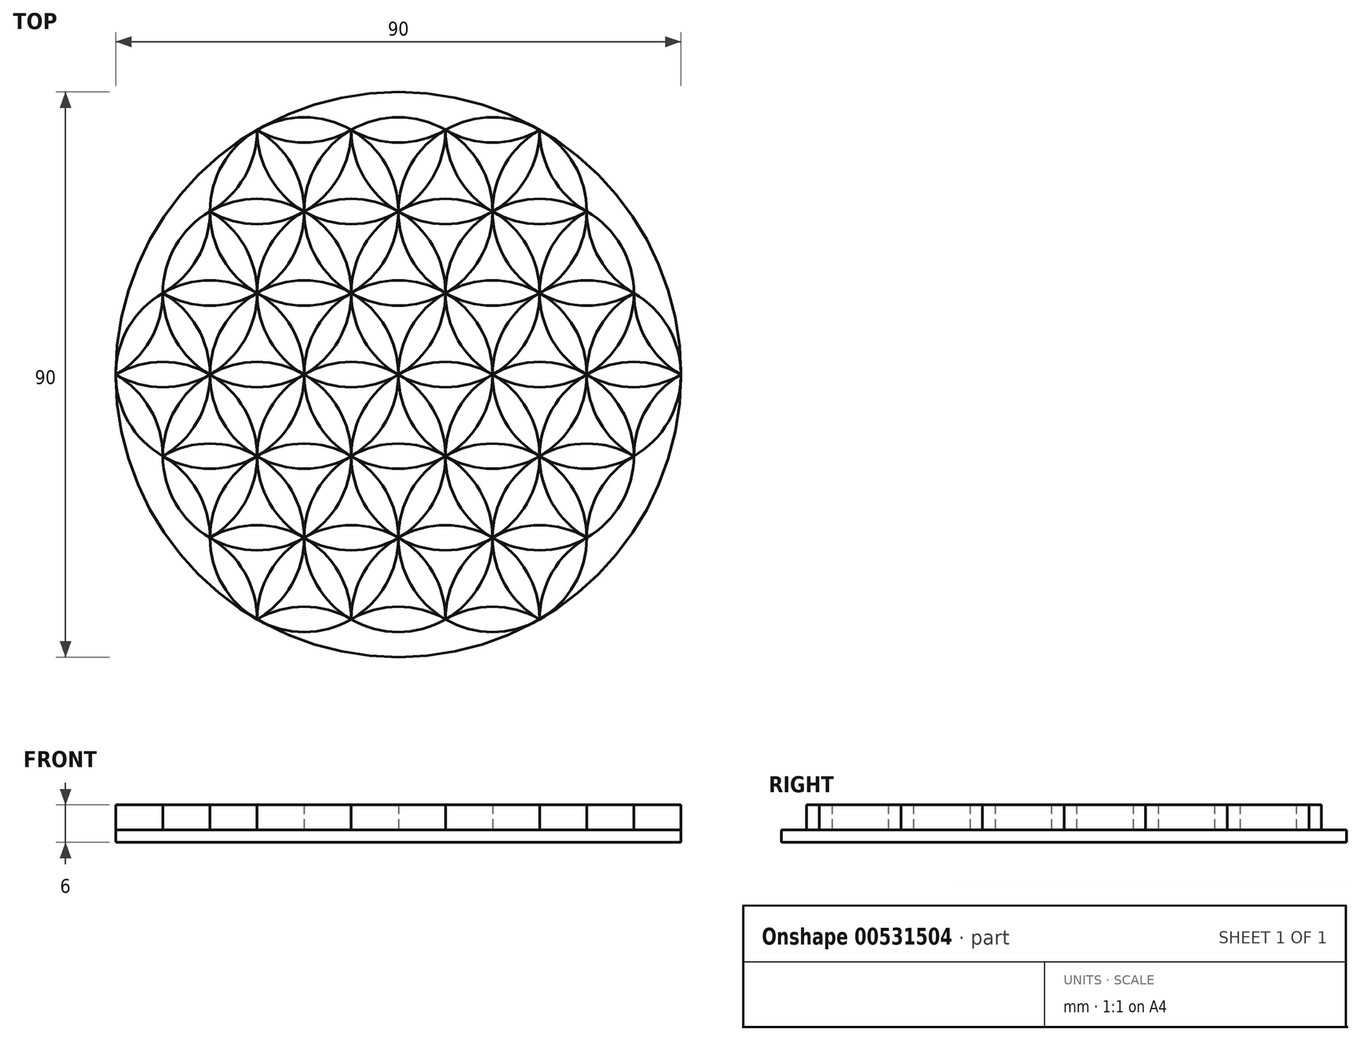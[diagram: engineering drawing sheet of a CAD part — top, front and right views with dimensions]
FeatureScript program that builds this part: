
annotation { "Feature Type Name" : "Feature", "Feature Type Description" : "" }
export const myFeature = defineFeature(function(context is Context, id is Id, definition is map)
    precondition{}
    {
        {
            var Q0;
            Q0=qCreatedBy(makeId("Top.planeOp"),FACE);
            var sketch = newSketch(context, id + "F0", { "sketchPlane" : qUnion([Q0])});
            skCircle(sketch, "E0", {"center": v(0, 0) * mm, "radius": 15 * mm});
            skCircle(sketch, "E1", {"center": v(15, 0) * mm, "radius": 15 * mm});
            skCircle(sketch, "E2", {"center": v(7.5, -13) * mm, "radius": 15 * mm});
            skCircle(sketch, "E3", {"center": v(-7.5, -13) * mm, "radius": 15 * mm});
            skCircle(sketch, "E4", {"center": v(-15, 0) * mm, "radius": 15 * mm});
            skCircle(sketch, "E5", {"center": v(-7.5, 13) * mm, "radius": 15 * mm});
            skCircle(sketch, "E6", {"center": v(7.5, 13) * mm, "radius": 15 * mm});
            skCircle(sketch, "E7", {"center": v(22.5, 13) * mm, "radius": 15 * mm});
            skCircle(sketch, "E8", {"center": v(-22.5, 13) * mm, "radius": 15 * mm});
            skCircle(sketch, "E9", {"center": v(-22.5, -13) * mm, "radius": 15 * mm});
            skCircle(sketch, "E10", {"center": v(-15, 25.98) * mm, "radius": 15 * mm});
            skCircle(sketch, "E11", {"center": v(0, 25.98) * mm, "radius": 15 * mm});
            skCircle(sketch, "E12", {"center": v(15, 25.98) * mm, "radius": 15 * mm});
            skCircle(sketch, "E13", {"center": v(7.5, 38.97) * mm, "radius": 15 * mm});
            skCircle(sketch, "E14", {"center": v(-7.5, 38.97) * mm, "radius": 15 * mm});
            skCircle(sketch, "E15", {"center": v(22.5, -13) * mm, "radius": 15 * mm});
            skCircle(sketch, "E16", {"center": v(30, 0) * mm, "radius": 15 * mm});
            skCircle(sketch, "E17", {"center": v(-30, 0) * mm, "radius": 15 * mm});
            skCircle(sketch, "E18", {"center": v(-15, -25.98) * mm, "radius": 15 * mm});
            skCircle(sketch, "E19", {"center": v(0, -25.98) * mm, "radius": 15 * mm});
            skCircle(sketch, "E20", {"center": v(15, -25.98) * mm, "radius": 15 * mm});
            skCircle(sketch, "E21", {"center": v(7.5, -38.97) * mm, "radius": 15 * mm});
            skCircle(sketch, "E22", {"center": v(-7.5, -38.97) * mm, "radius": 15 * mm});
            skCircle(sketch, "E23", {"center": v(30, -25.98) * mm, "radius": 15 * mm});
            skCircle(sketch, "E24", {"center": v(37.5, -13) * mm, "radius": 15 * mm});
            skCircle(sketch, "E25", {"center": v(-30, -25.98) * mm, "radius": 15 * mm});
            skCircle(sketch, "E26", {"center": v(-37.5, -13) * mm, "radius": 15 * mm});
            skCircle(sketch, "E27", {"center": v(-22.5, -38.97) * mm, "radius": 15 * mm});
            skCircle(sketch, "E28", {"center": v(22.5, -38.97) * mm, "radius": 15 * mm});
            skCircle(sketch, "E29", {"center": v(30, 25.98) * mm, "radius": 15 * mm});
            skCircle(sketch, "E30", {"center": v(37.5, 13) * mm, "radius": 15 * mm});
            skCircle(sketch, "E31", {"center": v(-30, 25.98) * mm, "radius": 15 * mm});
            skCircle(sketch, "E32", {"center": v(-37.5, 13) * mm, "radius": 15 * mm});
            skCircle(sketch, "E33", {"center": v(45, 0) * mm, "radius": 15 * mm});
            skCircle(sketch, "E34", {"center": v(45, -25.98) * mm, "radius": 15 * mm});
            skCircle(sketch, "E35", {"center": v(0, -51.96) * mm, "radius": 15 * mm});
            skCircle(sketch, "E36", {"center": v(0, 51.96) * mm, "radius": 15 * mm});
            skCircle(sketch, "E37", {"center": v(22.5, 38.97) * mm, "radius": 15 * mm});
            skCircle(sketch, "E38", {"center": v(-22.5, 38.97) * mm, "radius": 15 * mm});
            skCircle(sketch, "E39", {"center": v(-45, 0) * mm, "radius": 15 * mm});
            skCircle(sketch, "E40", {"center": v(-15, -51.96) * mm, "radius": 15 * mm});
            skCircle(sketch, "E41", {"center": v(15, -51.96) * mm, "radius": 15 * mm});
            skCircle(sketch, "E42", {"center": v(-45, -25.98) * mm, "radius": 15 * mm});
            skCircle(sketch, "E43", {"center": v(-37.5, -38.97) * mm, "radius": 15 * mm});
            skCircle(sketch, "E44", {"center": v(-52.5, 13) * mm, "radius": 15 * mm});
            skCircle(sketch, "E45", {"center": v(-45, 25.98) * mm, "radius": 15 * mm});
            skCircle(sketch, "E46", {"center": v(-37.5, 38.97) * mm, "radius": 15 * mm});
            skCircle(sketch, "E47", {"center": v(37.5, -38.97) * mm, "radius": 15 * mm});
            skCircle(sketch, "E48", {"center": v(-15, 51.96) * mm, "radius": 15 * mm});
            skCircle(sketch, "E49", {"center": v(-52.5, -13) * mm, "radius": 15 * mm});
            skCircle(sketch, "E50", {"center": v(15, 51.96) * mm, "radius": 15 * mm});
            skCircle(sketch, "E51", {"center": v(52.5, -13) * mm, "radius": 15 * mm});
            skCircle(sketch, "E52", {"center": v(37.5, 38.97) * mm, "radius": 15 * mm});
            skCircle(sketch, "E53", {"center": v(45, 25.98) * mm, "radius": 15 * mm});
            skCircle(sketch, "E54", {"center": v(52.5, 13) * mm, "radius": 15 * mm});
            skSolve(sketch);
        }
        {
            var Q0;
            {var subQ0=sQuery(id+"F0.wireOp",EDGE,"E6");var subQ1=sQuery(id+"F0.wireOp",EDGE,"E2");var subQ2=makeQuery(id+"F0.imprint","INTERSECT",VERTEX,{"derivedFrom":[sQuery(id+"F0.wireOp",EDGE,"E0"),subQ1,subQ0,sQuery(id+"F0.wireOp",EDGE,"E7"),sQuery(id+"F0.wireOp",EDGE,"E15"),sQuery(id+"F0.wireOp",EDGE,"E16")]});Q0=makeQuery(id+"F0.imprint","IMPRINT",FACE,{"disambiguationData":[TD([[makeQuery(id+"F0.imprint","IMPRINT",EDGE,{"disambiguationData":[TD([[subQ2,-1.0]])],"derivedFrom":subQ1}),1.0]])]});}
            var Q1;
            {var subQ0=sQuery(id+"F0.wireOp",EDGE,"E5");var subQ1=sQuery(id+"F0.wireOp",EDGE,"E1");var subQ2=makeQuery(id+"F0.imprint","INTERSECT",VERTEX,{"derivedFrom":[sQuery(id+"F0.wireOp",EDGE,"E0"),subQ1,subQ0,sQuery(id+"F0.wireOp",EDGE,"E7"),sQuery(id+"F0.wireOp",EDGE,"E11"),sQuery(id+"F0.wireOp",EDGE,"E12")]});Q1=makeQuery(id+"F0.imprint","IMPRINT",FACE,{"disambiguationData":[TD([[makeQuery(id+"F0.imprint","IMPRINT",EDGE,{"disambiguationData":[TD([[subQ2,-1.0]])],"derivedFrom":subQ1}),1.0]])]});}
            var Q2;
            {var subQ0=sQuery(id+"F0.wireOp",EDGE,"E6");var subQ1=sQuery(id+"F0.wireOp",EDGE,"E4");var subQ2=makeQuery(id+"F0.imprint","INTERSECT",VERTEX,{"derivedFrom":[sQuery(id+"F0.wireOp",EDGE,"E0"),subQ1,subQ0,sQuery(id+"F0.wireOp",EDGE,"E8"),sQuery(id+"F0.wireOp",EDGE,"E10"),sQuery(id+"F0.wireOp",EDGE,"E11")]});Q2=makeQuery(id+"F0.imprint","IMPRINT",FACE,{"disambiguationData":[TD([[makeQuery(id+"F0.imprint","IMPRINT",EDGE,{"disambiguationData":[TD([[subQ2,1.0]])],"derivedFrom":subQ1}),1.0]])]});}
            var Q3;
            {var subQ0=sQuery(id+"F0.wireOp",EDGE,"E5");var subQ1=sQuery(id+"F0.wireOp",EDGE,"E3");var subQ2=makeQuery(id+"F0.imprint","INTERSECT",VERTEX,{"derivedFrom":[sQuery(id+"F0.wireOp",EDGE,"E0"),subQ1,subQ0,sQuery(id+"F0.wireOp",EDGE,"E8"),sQuery(id+"F0.wireOp",EDGE,"E9"),sQuery(id+"F0.wireOp",EDGE,"E17")]});Q3=makeQuery(id+"F0.imprint","IMPRINT",FACE,{"disambiguationData":[TD([[makeQuery(id+"F0.imprint","IMPRINT",EDGE,{"disambiguationData":[TD([[subQ2,1.0]])],"derivedFrom":subQ1}),1.0]])]});}
            var Q4;
            {var subQ0=sQuery(id+"F0.wireOp",EDGE,"E4");var subQ1=sQuery(id+"F0.wireOp",EDGE,"E2");var subQ2=makeQuery(id+"F0.imprint","INTERSECT",VERTEX,{"derivedFrom":[sQuery(id+"F0.wireOp",EDGE,"E0"),subQ1,subQ0,sQuery(id+"F0.wireOp",EDGE,"E9"),sQuery(id+"F0.wireOp",EDGE,"E18"),sQuery(id+"F0.wireOp",EDGE,"E19")]});Q4=makeQuery(id+"F0.imprint","IMPRINT",FACE,{"disambiguationData":[TD([[makeQuery(id+"F0.imprint","IMPRINT",EDGE,{"disambiguationData":[TD([[subQ2,1.0]])],"derivedFrom":subQ1}),1.0]])]});}
            var Q5;
            {var subQ0=sQuery(id+"F0.wireOp",EDGE,"E3");var subQ1=sQuery(id+"F0.wireOp",EDGE,"E1");var subQ2=makeQuery(id+"F0.imprint","INTERSECT",VERTEX,{"derivedFrom":[sQuery(id+"F0.wireOp",EDGE,"E0"),subQ1,subQ0,sQuery(id+"F0.wireOp",EDGE,"E15"),sQuery(id+"F0.wireOp",EDGE,"E19"),sQuery(id+"F0.wireOp",EDGE,"E20")]});Q5=makeQuery(id+"F0.imprint","IMPRINT",FACE,{"disambiguationData":[TD([[makeQuery(id+"F0.imprint","IMPRINT",EDGE,{"disambiguationData":[TD([[subQ2,1.0]])],"derivedFrom":subQ1}),1.0]])]});}
            var Q6;
            {var subQ0=sQuery(id+"F0.wireOp",EDGE,"E15");var subQ1=sQuery(id+"F0.wireOp",EDGE,"E0");var subQ2=makeQuery(id+"F0.imprint","INTERSECT",VERTEX,{"derivedFrom":[subQ1,sQuery(id+"F0.wireOp",EDGE,"E2"),sQuery(id+"F0.wireOp",EDGE,"E6"),sQuery(id+"F0.wireOp",EDGE,"E7"),subQ0,sQuery(id+"F0.wireOp",EDGE,"E16")]});Q6=makeQuery(id+"F0.imprint","IMPRINT",FACE,{"disambiguationData":[TD([[makeQuery(id+"F0.imprint","IMPRINT",EDGE,{"disambiguationData":[TD([[subQ2,1.0]])],"derivedFrom":subQ1}),1.0]])]});}
            var Q7;
            {var subQ0=sQuery(id+"F0.wireOp",EDGE,"E7");var subQ1=sQuery(id+"F0.wireOp",EDGE,"E0");var subQ2=makeQuery(id+"F0.imprint","INTERSECT",VERTEX,{"derivedFrom":[subQ1,sQuery(id+"F0.wireOp",EDGE,"E1"),sQuery(id+"F0.wireOp",EDGE,"E5"),subQ0,sQuery(id+"F0.wireOp",EDGE,"E11"),sQuery(id+"F0.wireOp",EDGE,"E12")]});Q7=makeQuery(id+"F0.imprint","IMPRINT",FACE,{"disambiguationData":[TD([[makeQuery(id+"F0.imprint","IMPRINT",EDGE,{"disambiguationData":[TD([[subQ2,1.0]])],"derivedFrom":subQ1}),1.0]])]});}
            var Q8;
            {var subQ0=sQuery(id+"F0.wireOp",EDGE,"E11");var subQ1=sQuery(id+"F0.wireOp",EDGE,"E0");var subQ2=makeQuery(id+"F0.imprint","INTERSECT",VERTEX,{"derivedFrom":[subQ1,sQuery(id+"F0.wireOp",EDGE,"E1"),sQuery(id+"F0.wireOp",EDGE,"E5"),sQuery(id+"F0.wireOp",EDGE,"E7"),subQ0,sQuery(id+"F0.wireOp",EDGE,"E12")]});Q8=makeQuery(id+"F0.imprint","IMPRINT",FACE,{"disambiguationData":[TD([[makeQuery(id+"F0.imprint","IMPRINT",EDGE,{"disambiguationData":[TD([[subQ2,-1.0]])],"derivedFrom":subQ1}),1.0]])]});}
            var Q9;
            {var subQ0=sQuery(id+"F0.wireOp",EDGE,"E8");var subQ1=sQuery(id+"F0.wireOp",EDGE,"E0");var subQ2=makeQuery(id+"F0.imprint","INTERSECT",VERTEX,{"derivedFrom":[subQ1,sQuery(id+"F0.wireOp",EDGE,"E4"),sQuery(id+"F0.wireOp",EDGE,"E6"),subQ0,sQuery(id+"F0.wireOp",EDGE,"E10"),sQuery(id+"F0.wireOp",EDGE,"E11")]});Q9=makeQuery(id+"F0.imprint","IMPRINT",FACE,{"disambiguationData":[TD([[makeQuery(id+"F0.imprint","IMPRINT",EDGE,{"disambiguationData":[TD([[subQ2,-1.0]])],"derivedFrom":subQ1}),1.0]])]});}
            var Q10;
            {var subQ0=sQuery(id+"F0.wireOp",EDGE,"E9");var subQ1=sQuery(id+"F0.wireOp",EDGE,"E0");var subQ2=makeQuery(id+"F0.imprint","INTERSECT",VERTEX,{"derivedFrom":[subQ1,sQuery(id+"F0.wireOp",EDGE,"E3"),sQuery(id+"F0.wireOp",EDGE,"E5"),sQuery(id+"F0.wireOp",EDGE,"E8"),subQ0,sQuery(id+"F0.wireOp",EDGE,"E17")]});Q10=makeQuery(id+"F0.imprint","IMPRINT",FACE,{"disambiguationData":[TD([[makeQuery(id+"F0.imprint","IMPRINT",EDGE,{"disambiguationData":[TD([[subQ2,-1.0]])],"derivedFrom":subQ1}),1.0]])]});}
            var Q11;
            {var subQ0=sQuery(id+"F0.wireOp",EDGE,"E19");var subQ1=sQuery(id+"F0.wireOp",EDGE,"E0");var subQ2=makeQuery(id+"F0.imprint","INTERSECT",VERTEX,{"derivedFrom":[subQ1,sQuery(id+"F0.wireOp",EDGE,"E2"),sQuery(id+"F0.wireOp",EDGE,"E4"),sQuery(id+"F0.wireOp",EDGE,"E9"),sQuery(id+"F0.wireOp",EDGE,"E18"),subQ0]});Q11=makeQuery(id+"F0.imprint","IMPRINT",FACE,{"disambiguationData":[TD([[makeQuery(id+"F0.imprint","IMPRINT",EDGE,{"disambiguationData":[TD([[subQ2,-1.0]])],"derivedFrom":subQ1}),1.0]])]});}
            var Q12;
            {var subQ0=sQuery(id+"F0.wireOp",EDGE,"E18");var subQ1=sQuery(id+"F0.wireOp",EDGE,"E4");var subQ2=makeQuery(id+"F0.imprint","INTERSECT",VERTEX,{"derivedFrom":[sQuery(id+"F0.wireOp",EDGE,"E0"),sQuery(id+"F0.wireOp",EDGE,"E2"),subQ1,sQuery(id+"F0.wireOp",EDGE,"E9"),subQ0,sQuery(id+"F0.wireOp",EDGE,"E19")]});Q12=makeQuery(id+"F0.imprint","IMPRINT",FACE,{"disambiguationData":[TD([[makeQuery(id+"F0.imprint","IMPRINT",EDGE,{"disambiguationData":[TD([[subQ2,1.0]])],"derivedFrom":subQ1}),1.0]])]});}
            var Q13;
            {var subQ0=sQuery(id+"F0.wireOp",EDGE,"E19");var subQ1=sQuery(id+"F0.wireOp",EDGE,"E9");var subQ2=makeQuery(id+"F0.imprint","INTERSECT",VERTEX,{"derivedFrom":[sQuery(id+"F0.wireOp",EDGE,"E0"),sQuery(id+"F0.wireOp",EDGE,"E2"),sQuery(id+"F0.wireOp",EDGE,"E4"),subQ1,sQuery(id+"F0.wireOp",EDGE,"E18"),subQ0]});Q13=makeQuery(id+"F0.imprint","IMPRINT",FACE,{"disambiguationData":[TD([[makeQuery(id+"F0.imprint","IMPRINT",EDGE,{"disambiguationData":[TD([[subQ2,1.0]])],"derivedFrom":subQ1}),1.0]])]});}
            var Q14;
            {var subQ0=sQuery(id+"F0.wireOp",EDGE,"E18");var subQ1=sQuery(id+"F0.wireOp",EDGE,"E2");var subQ2=makeQuery(id+"F0.imprint","INTERSECT",VERTEX,{"derivedFrom":[sQuery(id+"F0.wireOp",EDGE,"E0"),subQ1,sQuery(id+"F0.wireOp",EDGE,"E4"),sQuery(id+"F0.wireOp",EDGE,"E9"),subQ0,sQuery(id+"F0.wireOp",EDGE,"E19")]});Q14=makeQuery(id+"F0.imprint","IMPRINT",FACE,{"disambiguationData":[TD([[makeQuery(id+"F0.imprint","IMPRINT",EDGE,{"disambiguationData":[TD([[subQ2,-1.0]])],"derivedFrom":subQ1}),1.0]])]});}
            var Q15;
            {var subQ0=sQuery(id+"F0.wireOp",EDGE,"E20");var subQ1=sQuery(id+"F0.wireOp",EDGE,"E3");var subQ2=makeQuery(id+"F0.imprint","INTERSECT",VERTEX,{"derivedFrom":[sQuery(id+"F0.wireOp",EDGE,"E0"),sQuery(id+"F0.wireOp",EDGE,"E1"),subQ1,sQuery(id+"F0.wireOp",EDGE,"E15"),sQuery(id+"F0.wireOp",EDGE,"E19"),subQ0]});Q15=makeQuery(id+"F0.imprint","IMPRINT",FACE,{"disambiguationData":[TD([[makeQuery(id+"F0.imprint","IMPRINT",EDGE,{"disambiguationData":[TD([[subQ2,1.0]])],"derivedFrom":subQ1}),1.0]])]});}
            var Q16;
            {var subQ0=sQuery(id+"F0.wireOp",EDGE,"E19");var subQ1=sQuery(id+"F0.wireOp",EDGE,"E15");var subQ2=makeQuery(id+"F0.imprint","INTERSECT",VERTEX,{"derivedFrom":[sQuery(id+"F0.wireOp",EDGE,"E0"),sQuery(id+"F0.wireOp",EDGE,"E1"),sQuery(id+"F0.wireOp",EDGE,"E3"),subQ1,subQ0,sQuery(id+"F0.wireOp",EDGE,"E20")]});Q16=makeQuery(id+"F0.imprint","IMPRINT",FACE,{"disambiguationData":[TD([[makeQuery(id+"F0.imprint","IMPRINT",EDGE,{"disambiguationData":[TD([[subQ2,-1.0]])],"derivedFrom":subQ1}),1.0]])]});}
            var Q17;
            {var subQ0=sQuery(id+"F0.wireOp",EDGE,"E20");var subQ1=sQuery(id+"F0.wireOp",EDGE,"E1");var subQ2=makeQuery(id+"F0.imprint","INTERSECT",VERTEX,{"derivedFrom":[sQuery(id+"F0.wireOp",EDGE,"E0"),subQ1,sQuery(id+"F0.wireOp",EDGE,"E3"),sQuery(id+"F0.wireOp",EDGE,"E15"),sQuery(id+"F0.wireOp",EDGE,"E19"),subQ0]});Q17=makeQuery(id+"F0.imprint","IMPRINT",FACE,{"disambiguationData":[TD([[makeQuery(id+"F0.imprint","IMPRINT",EDGE,{"disambiguationData":[TD([[subQ2,-1.0]])],"derivedFrom":subQ1}),1.0]])]});}
            var Q18;
            {var subQ0=sQuery(id+"F0.wireOp",EDGE,"E16");var subQ1=sQuery(id+"F0.wireOp",EDGE,"E2");var subQ2=makeQuery(id+"F0.imprint","INTERSECT",VERTEX,{"derivedFrom":[sQuery(id+"F0.wireOp",EDGE,"E0"),subQ1,sQuery(id+"F0.wireOp",EDGE,"E6"),sQuery(id+"F0.wireOp",EDGE,"E7"),sQuery(id+"F0.wireOp",EDGE,"E15"),subQ0]});Q18=makeQuery(id+"F0.imprint","IMPRINT",FACE,{"disambiguationData":[TD([[makeQuery(id+"F0.imprint","IMPRINT",EDGE,{"disambiguationData":[TD([[subQ2,1.0]])],"derivedFrom":subQ1}),1.0]])]});}
            var Q19;
            {var subQ0=sQuery(id+"F0.wireOp",EDGE,"E15");var subQ1=sQuery(id+"F0.wireOp",EDGE,"E7");var subQ2=makeQuery(id+"F0.imprint","INTERSECT",VERTEX,{"derivedFrom":[sQuery(id+"F0.wireOp",EDGE,"E0"),sQuery(id+"F0.wireOp",EDGE,"E2"),sQuery(id+"F0.wireOp",EDGE,"E6"),subQ1,subQ0,sQuery(id+"F0.wireOp",EDGE,"E16")]});Q19=makeQuery(id+"F0.imprint","IMPRINT",FACE,{"disambiguationData":[TD([[makeQuery(id+"F0.imprint","IMPRINT",EDGE,{"disambiguationData":[TD([[subQ2,-1.0]])],"derivedFrom":subQ1}),1.0]])]});}
            var Q20;
            {var subQ0=sQuery(id+"F0.wireOp",EDGE,"E16");var subQ1=sQuery(id+"F0.wireOp",EDGE,"E6");var subQ2=makeQuery(id+"F0.imprint","INTERSECT",VERTEX,{"derivedFrom":[sQuery(id+"F0.wireOp",EDGE,"E0"),sQuery(id+"F0.wireOp",EDGE,"E2"),subQ1,sQuery(id+"F0.wireOp",EDGE,"E7"),sQuery(id+"F0.wireOp",EDGE,"E15"),subQ0]});Q20=makeQuery(id+"F0.imprint","IMPRINT",FACE,{"disambiguationData":[TD([[makeQuery(id+"F0.imprint","IMPRINT",EDGE,{"disambiguationData":[TD([[subQ2,-1.0]])],"derivedFrom":subQ1}),1.0]])]});}
            var Q21;
            {var subQ0=sQuery(id+"F0.wireOp",EDGE,"E12");var subQ1=sQuery(id+"F0.wireOp",EDGE,"E1");var subQ2=makeQuery(id+"F0.imprint","INTERSECT",VERTEX,{"derivedFrom":[sQuery(id+"F0.wireOp",EDGE,"E0"),subQ1,sQuery(id+"F0.wireOp",EDGE,"E5"),sQuery(id+"F0.wireOp",EDGE,"E7"),sQuery(id+"F0.wireOp",EDGE,"E11"),subQ0]});Q21=makeQuery(id+"F0.imprint","IMPRINT",FACE,{"disambiguationData":[TD([[makeQuery(id+"F0.imprint","IMPRINT",EDGE,{"disambiguationData":[TD([[subQ2,1.0]])],"derivedFrom":subQ1}),1.0]])]});}
            var Q22;
            {var subQ0=sQuery(id+"F0.wireOp",EDGE,"E11");var subQ1=sQuery(id+"F0.wireOp",EDGE,"E7");var subQ2=makeQuery(id+"F0.imprint","INTERSECT",VERTEX,{"derivedFrom":[sQuery(id+"F0.wireOp",EDGE,"E0"),sQuery(id+"F0.wireOp",EDGE,"E1"),sQuery(id+"F0.wireOp",EDGE,"E5"),subQ1,subQ0,sQuery(id+"F0.wireOp",EDGE,"E12")]});Q22=makeQuery(id+"F0.imprint","IMPRINT",FACE,{"disambiguationData":[TD([[makeQuery(id+"F0.imprint","IMPRINT",EDGE,{"disambiguationData":[TD([[subQ2,1.0]])],"derivedFrom":subQ1}),1.0]])]});}
            var Q23;
            {var subQ0=sQuery(id+"F0.wireOp",EDGE,"E12");var subQ1=sQuery(id+"F0.wireOp",EDGE,"E5");var subQ2=makeQuery(id+"F0.imprint","INTERSECT",VERTEX,{"derivedFrom":[sQuery(id+"F0.wireOp",EDGE,"E0"),sQuery(id+"F0.wireOp",EDGE,"E1"),subQ1,sQuery(id+"F0.wireOp",EDGE,"E7"),sQuery(id+"F0.wireOp",EDGE,"E11"),subQ0]});Q23=makeQuery(id+"F0.imprint","IMPRINT",FACE,{"disambiguationData":[TD([[makeQuery(id+"F0.imprint","IMPRINT",EDGE,{"disambiguationData":[TD([[subQ2,-1.0]])],"derivedFrom":subQ1}),1.0]])]});}
            var Q24;
            {var subQ0=sQuery(id+"F0.wireOp",EDGE,"E10");var subQ1=sQuery(id+"F0.wireOp",EDGE,"E6");var subQ2=makeQuery(id+"F0.imprint","INTERSECT",VERTEX,{"derivedFrom":[sQuery(id+"F0.wireOp",EDGE,"E0"),sQuery(id+"F0.wireOp",EDGE,"E4"),subQ1,sQuery(id+"F0.wireOp",EDGE,"E8"),subQ0,sQuery(id+"F0.wireOp",EDGE,"E11")]});Q24=makeQuery(id+"F0.imprint","IMPRINT",FACE,{"disambiguationData":[TD([[makeQuery(id+"F0.imprint","IMPRINT",EDGE,{"disambiguationData":[TD([[subQ2,1.0]])],"derivedFrom":subQ1}),1.0]])]});}
            var Q25;
            {var subQ0=sQuery(id+"F0.wireOp",EDGE,"E11");var subQ1=sQuery(id+"F0.wireOp",EDGE,"E8");var subQ2=makeQuery(id+"F0.imprint","INTERSECT",VERTEX,{"derivedFrom":[sQuery(id+"F0.wireOp",EDGE,"E0"),sQuery(id+"F0.wireOp",EDGE,"E4"),sQuery(id+"F0.wireOp",EDGE,"E6"),subQ1,sQuery(id+"F0.wireOp",EDGE,"E10"),subQ0]});Q25=makeQuery(id+"F0.imprint","IMPRINT",FACE,{"disambiguationData":[TD([[makeQuery(id+"F0.imprint","IMPRINT",EDGE,{"disambiguationData":[TD([[subQ2,-1.0]])],"derivedFrom":subQ1}),1.0]])]});}
            var Q26;
            {var subQ0=sQuery(id+"F0.wireOp",EDGE,"E10");var subQ1=sQuery(id+"F0.wireOp",EDGE,"E4");var subQ2=makeQuery(id+"F0.imprint","INTERSECT",VERTEX,{"derivedFrom":[sQuery(id+"F0.wireOp",EDGE,"E0"),subQ1,sQuery(id+"F0.wireOp",EDGE,"E6"),sQuery(id+"F0.wireOp",EDGE,"E8"),subQ0,sQuery(id+"F0.wireOp",EDGE,"E11")]});Q26=makeQuery(id+"F0.imprint","IMPRINT",FACE,{"disambiguationData":[TD([[makeQuery(id+"F0.imprint","IMPRINT",EDGE,{"disambiguationData":[TD([[subQ2,-1.0]])],"derivedFrom":subQ1}),1.0]])]});}
            var Q27;
            {var subQ0=sQuery(id+"F0.wireOp",EDGE,"E17");var subQ1=sQuery(id+"F0.wireOp",EDGE,"E5");var subQ2=makeQuery(id+"F0.imprint","INTERSECT",VERTEX,{"derivedFrom":[sQuery(id+"F0.wireOp",EDGE,"E0"),sQuery(id+"F0.wireOp",EDGE,"E3"),subQ1,sQuery(id+"F0.wireOp",EDGE,"E8"),sQuery(id+"F0.wireOp",EDGE,"E9"),subQ0]});Q27=makeQuery(id+"F0.imprint","IMPRINT",FACE,{"disambiguationData":[TD([[makeQuery(id+"F0.imprint","IMPRINT",EDGE,{"disambiguationData":[TD([[subQ2,1.0]])],"derivedFrom":subQ1}),1.0]])]});}
            var Q28;
            {var subQ0=sQuery(id+"F0.wireOp",EDGE,"E9");var subQ1=sQuery(id+"F0.wireOp",EDGE,"E8");var subQ2=makeQuery(id+"F0.imprint","INTERSECT",VERTEX,{"derivedFrom":[sQuery(id+"F0.wireOp",EDGE,"E0"),sQuery(id+"F0.wireOp",EDGE,"E3"),sQuery(id+"F0.wireOp",EDGE,"E5"),subQ1,subQ0,sQuery(id+"F0.wireOp",EDGE,"E17")]});Q28=makeQuery(id+"F0.imprint","IMPRINT",FACE,{"disambiguationData":[TD([[makeQuery(id+"F0.imprint","IMPRINT",EDGE,{"disambiguationData":[TD([[subQ2,1.0]])],"derivedFrom":subQ1}),1.0]])]});}
            var Q29;
            {var subQ0=sQuery(id+"F0.wireOp",EDGE,"E17");var subQ1=sQuery(id+"F0.wireOp",EDGE,"E3");var subQ2=makeQuery(id+"F0.imprint","INTERSECT",VERTEX,{"derivedFrom":[sQuery(id+"F0.wireOp",EDGE,"E0"),subQ1,sQuery(id+"F0.wireOp",EDGE,"E5"),sQuery(id+"F0.wireOp",EDGE,"E8"),sQuery(id+"F0.wireOp",EDGE,"E9"),subQ0]});Q29=makeQuery(id+"F0.imprint","IMPRINT",FACE,{"disambiguationData":[TD([[makeQuery(id+"F0.imprint","IMPRINT",EDGE,{"disambiguationData":[TD([[subQ2,-1.0]])],"derivedFrom":subQ1}),1.0]])]});}
            var Q30;
            {var subQ0=sQuery(id+"F0.wireOp",EDGE,"E26");var subQ1=sQuery(id+"F0.wireOp",EDGE,"E4");var subQ2=makeQuery(id+"F0.imprint","INTERSECT",VERTEX,{"derivedFrom":[sQuery(id+"F0.wireOp",EDGE,"E3"),subQ1,sQuery(id+"F0.wireOp",EDGE,"E17"),sQuery(id+"F0.wireOp",EDGE,"E18"),sQuery(id+"F0.wireOp",EDGE,"E25"),subQ0]});Q30=makeQuery(id+"F0.imprint","IMPRINT",FACE,{"disambiguationData":[TD([[makeQuery(id+"F0.imprint","IMPRINT",EDGE,{"disambiguationData":[TD([[subQ2,1.0]])],"derivedFrom":subQ1}),1.0]])]});}
            var Q31;
            {var subQ0=sQuery(id+"F0.wireOp",EDGE,"E25");var subQ1=sQuery(id+"F0.wireOp",EDGE,"E3");var subQ2=makeQuery(id+"F0.imprint","INTERSECT",VERTEX,{"derivedFrom":[subQ1,sQuery(id+"F0.wireOp",EDGE,"E4"),sQuery(id+"F0.wireOp",EDGE,"E17"),sQuery(id+"F0.wireOp",EDGE,"E18"),subQ0,sQuery(id+"F0.wireOp",EDGE,"E26")]});Q31=makeQuery(id+"F0.imprint","IMPRINT",FACE,{"disambiguationData":[TD([[makeQuery(id+"F0.imprint","IMPRINT",EDGE,{"disambiguationData":[TD([[subQ2,-1.0]])],"derivedFrom":subQ1}),1.0]])]});}
            var Q32;
            {var subQ0=sQuery(id+"F0.wireOp",EDGE,"E22");var subQ1=sQuery(id+"F0.wireOp",EDGE,"E3");var subQ2=makeQuery(id+"F0.imprint","INTERSECT",VERTEX,{"derivedFrom":[sQuery(id+"F0.wireOp",EDGE,"E2"),subQ1,sQuery(id+"F0.wireOp",EDGE,"E18"),sQuery(id+"F0.wireOp",EDGE,"E20"),sQuery(id+"F0.wireOp",EDGE,"E21"),subQ0]});Q32=makeQuery(id+"F0.imprint","IMPRINT",FACE,{"disambiguationData":[TD([[makeQuery(id+"F0.imprint","IMPRINT",EDGE,{"disambiguationData":[TD([[subQ2,1.0]])],"derivedFrom":subQ1}),1.0]])]});}
            var Q33;
            {var subQ0=sQuery(id+"F0.wireOp",EDGE,"E21");var subQ1=sQuery(id+"F0.wireOp",EDGE,"E18");var subQ2=makeQuery(id+"F0.imprint","INTERSECT",VERTEX,{"derivedFrom":[sQuery(id+"F0.wireOp",EDGE,"E2"),sQuery(id+"F0.wireOp",EDGE,"E3"),subQ1,sQuery(id+"F0.wireOp",EDGE,"E20"),subQ0,sQuery(id+"F0.wireOp",EDGE,"E22")]});Q33=makeQuery(id+"F0.imprint","IMPRINT",FACE,{"disambiguationData":[TD([[makeQuery(id+"F0.imprint","IMPRINT",EDGE,{"disambiguationData":[TD([[subQ2,1.0]])],"derivedFrom":subQ1}),1.0]])]});}
            var Q34;
            {var subQ0=sQuery(id+"F0.wireOp",EDGE,"E21");var subQ1=sQuery(id+"F0.wireOp",EDGE,"E2");var subQ2=makeQuery(id+"F0.imprint","INTERSECT",VERTEX,{"derivedFrom":[subQ1,sQuery(id+"F0.wireOp",EDGE,"E3"),sQuery(id+"F0.wireOp",EDGE,"E18"),sQuery(id+"F0.wireOp",EDGE,"E20"),subQ0,sQuery(id+"F0.wireOp",EDGE,"E22")]});Q34=makeQuery(id+"F0.imprint","IMPRINT",FACE,{"disambiguationData":[TD([[makeQuery(id+"F0.imprint","IMPRINT",EDGE,{"disambiguationData":[TD([[subQ2,-1.0]])],"derivedFrom":subQ1}),1.0]])]});}
            var Q35;
            {var subQ0=sQuery(id+"F0.wireOp",EDGE,"E13");var subQ1=sQuery(id+"F0.wireOp",EDGE,"E6");var subQ2=makeQuery(id+"F0.imprint","INTERSECT",VERTEX,{"derivedFrom":[sQuery(id+"F0.wireOp",EDGE,"E5"),subQ1,sQuery(id+"F0.wireOp",EDGE,"E10"),sQuery(id+"F0.wireOp",EDGE,"E12"),subQ0,sQuery(id+"F0.wireOp",EDGE,"E14")]});Q35=makeQuery(id+"F0.imprint","IMPRINT",FACE,{"disambiguationData":[TD([[makeQuery(id+"F0.imprint","IMPRINT",EDGE,{"disambiguationData":[TD([[subQ2,1.0]])],"derivedFrom":subQ1}),1.0]])]});}
            var Q36;
            {var subQ0=sQuery(id+"F0.wireOp",EDGE,"E14");var subQ1=sQuery(id+"F0.wireOp",EDGE,"E12");var subQ2=makeQuery(id+"F0.imprint","INTERSECT",VERTEX,{"derivedFrom":[sQuery(id+"F0.wireOp",EDGE,"E11"),subQ1,subQ0,sQuery(id+"F0.wireOp",EDGE,"E36"),sQuery(id+"F0.wireOp",EDGE,"E37")]});Q36=makeQuery(id+"F0.imprint","IMPRINT",FACE,{"disambiguationData":[TD([[makeQuery(id+"F0.imprint","IMPRINT",EDGE,{"disambiguationData":[TD([[subQ2,-1.0]])],"derivedFrom":subQ1}),1.0]])]});}
            var Q37;
            {var subQ0=sQuery(id+"F0.wireOp",EDGE,"E13");var subQ1=sQuery(id+"F0.wireOp",EDGE,"E10");var subQ2=makeQuery(id+"F0.imprint","INTERSECT",VERTEX,{"derivedFrom":[subQ1,sQuery(id+"F0.wireOp",EDGE,"E11"),subQ0,sQuery(id+"F0.wireOp",EDGE,"E36"),sQuery(id+"F0.wireOp",EDGE,"E38")]});Q37=makeQuery(id+"F0.imprint","IMPRINT",FACE,{"disambiguationData":[TD([[makeQuery(id+"F0.imprint","IMPRINT",EDGE,{"disambiguationData":[TD([[subQ2,1.0]])],"derivedFrom":subQ1}),1.0]])]});}
            var Q38;
            {var subQ0=sQuery(id+"F0.wireOp",EDGE,"E14");var subQ1=sQuery(id+"F0.wireOp",EDGE,"E5");var subQ2=makeQuery(id+"F0.imprint","INTERSECT",VERTEX,{"derivedFrom":[subQ1,sQuery(id+"F0.wireOp",EDGE,"E6"),sQuery(id+"F0.wireOp",EDGE,"E10"),sQuery(id+"F0.wireOp",EDGE,"E12"),sQuery(id+"F0.wireOp",EDGE,"E13"),subQ0]});Q38=makeQuery(id+"F0.imprint","IMPRINT",FACE,{"disambiguationData":[TD([[makeQuery(id+"F0.imprint","IMPRINT",EDGE,{"disambiguationData":[TD([[subQ2,-1.0]])],"derivedFrom":subQ1}),1.0]])]});}
            var Q39;
            {var subQ0=sQuery(id+"F0.wireOp",EDGE,"E36");var subQ1=sQuery(id+"F0.wireOp",EDGE,"E11");var subQ2=makeQuery(id+"F0.imprint","INTERSECT",VERTEX,{"derivedFrom":[sQuery(id+"F0.wireOp",EDGE,"E10"),subQ1,sQuery(id+"F0.wireOp",EDGE,"E13"),subQ0,sQuery(id+"F0.wireOp",EDGE,"E38")]});Q39=makeQuery(id+"F0.imprint","IMPRINT",FACE,{"disambiguationData":[TD([[makeQuery(id+"F0.imprint","IMPRINT",EDGE,{"disambiguationData":[TD([[subQ2,1.0]])],"derivedFrom":subQ1}),1.0]])]});}
            var Q40;
            {var subQ0=sQuery(id+"F0.wireOp",EDGE,"E37");var subQ1=sQuery(id+"F0.wireOp",EDGE,"E11");var subQ2=makeQuery(id+"F0.imprint","INTERSECT",VERTEX,{"derivedFrom":[subQ1,sQuery(id+"F0.wireOp",EDGE,"E12"),sQuery(id+"F0.wireOp",EDGE,"E14"),sQuery(id+"F0.wireOp",EDGE,"E36"),subQ0]});Q40=makeQuery(id+"F0.imprint","IMPRINT",FACE,{"disambiguationData":[TD([[makeQuery(id+"F0.imprint","IMPRINT",EDGE,{"disambiguationData":[TD([[subQ2,1.0]])],"derivedFrom":subQ1}),1.0]])]});}
            var Q41;
            {var subQ0=sQuery(id+"F0.wireOp",EDGE,"E29");var subQ1=sQuery(id+"F0.wireOp",EDGE,"E6");var subQ2=makeQuery(id+"F0.imprint","INTERSECT",VERTEX,{"derivedFrom":[sQuery(id+"F0.wireOp",EDGE,"E1"),subQ1,sQuery(id+"F0.wireOp",EDGE,"E12"),sQuery(id+"F0.wireOp",EDGE,"E16"),subQ0,sQuery(id+"F0.wireOp",EDGE,"E30")]});Q41=makeQuery(id+"F0.imprint","IMPRINT",FACE,{"disambiguationData":[TD([[makeQuery(id+"F0.imprint","IMPRINT",EDGE,{"disambiguationData":[TD([[subQ2,-1.0]])],"derivedFrom":subQ1}),1.0]])]});}
            var Q42;
            {var subQ0=sQuery(id+"F0.wireOp",EDGE,"E30");var subQ1=sQuery(id+"F0.wireOp",EDGE,"E1");var subQ2=makeQuery(id+"F0.imprint","INTERSECT",VERTEX,{"derivedFrom":[subQ1,sQuery(id+"F0.wireOp",EDGE,"E6"),sQuery(id+"F0.wireOp",EDGE,"E12"),sQuery(id+"F0.wireOp",EDGE,"E16"),sQuery(id+"F0.wireOp",EDGE,"E29"),subQ0]});Q42=makeQuery(id+"F0.imprint","IMPRINT",FACE,{"disambiguationData":[TD([[makeQuery(id+"F0.imprint","IMPRINT",EDGE,{"disambiguationData":[TD([[subQ2,1.0]])],"derivedFrom":subQ1}),1.0]])]});}
            var Q43;
            {var subQ0=sQuery(id+"F0.wireOp",EDGE,"E24");var subQ1=sQuery(id+"F0.wireOp",EDGE,"E1");var subQ2=makeQuery(id+"F0.imprint","INTERSECT",VERTEX,{"derivedFrom":[subQ1,sQuery(id+"F0.wireOp",EDGE,"E7"),sQuery(id+"F0.wireOp",EDGE,"E15"),subQ0,sQuery(id+"F0.wireOp",EDGE,"E30"),sQuery(id+"F0.wireOp",EDGE,"E33")]});Q43=makeQuery(id+"F0.imprint","IMPRINT",FACE,{"disambiguationData":[TD([[makeQuery(id+"F0.imprint","IMPRINT",EDGE,{"disambiguationData":[TD([[subQ2,1.0]])],"derivedFrom":subQ1}),1.0]])]});}
            var Q44;
            {var subQ0=sQuery(id+"F0.wireOp",EDGE,"E23");var subQ1=sQuery(id+"F0.wireOp",EDGE,"E2");var subQ2=makeQuery(id+"F0.imprint","INTERSECT",VERTEX,{"derivedFrom":[sQuery(id+"F0.wireOp",EDGE,"E1"),subQ1,sQuery(id+"F0.wireOp",EDGE,"E16"),sQuery(id+"F0.wireOp",EDGE,"E20"),subQ0,sQuery(id+"F0.wireOp",EDGE,"E24")]});Q44=makeQuery(id+"F0.imprint","IMPRINT",FACE,{"disambiguationData":[TD([[makeQuery(id+"F0.imprint","IMPRINT",EDGE,{"disambiguationData":[TD([[subQ2,1.0]])],"derivedFrom":subQ1}),1.0]])]});}
            var Q45;
            {var subQ0=sQuery(id+"F0.wireOp",EDGE,"E28");var subQ1=sQuery(id+"F0.wireOp",EDGE,"E19");var subQ2=makeQuery(id+"F0.imprint","INTERSECT",VERTEX,{"derivedFrom":[sQuery(id+"F0.wireOp",EDGE,"E2"),sQuery(id+"F0.wireOp",EDGE,"E15"),subQ1,sQuery(id+"F0.wireOp",EDGE,"E21"),sQuery(id+"F0.wireOp",EDGE,"E23"),subQ0]});Q45=makeQuery(id+"F0.imprint","IMPRINT",FACE,{"disambiguationData":[TD([[makeQuery(id+"F0.imprint","IMPRINT",EDGE,{"disambiguationData":[TD([[subQ2,1.0]])],"derivedFrom":subQ1}),1.0]])]});}
            var Q46;
            {var subQ0=sQuery(id+"F0.wireOp",EDGE,"E22");var subQ1=sQuery(id+"F0.wireOp",EDGE,"E20");var subQ2=makeQuery(id+"F0.imprint","INTERSECT",VERTEX,{"derivedFrom":[sQuery(id+"F0.wireOp",EDGE,"E2"),sQuery(id+"F0.wireOp",EDGE,"E3"),sQuery(id+"F0.wireOp",EDGE,"E18"),subQ1,sQuery(id+"F0.wireOp",EDGE,"E21"),subQ0]});Q46=makeQuery(id+"F0.imprint","IMPRINT",FACE,{"disambiguationData":[TD([[makeQuery(id+"F0.imprint","IMPRINT",EDGE,{"disambiguationData":[TD([[subQ2,-1.0]])],"derivedFrom":subQ1}),1.0]])]});}
            var Q47;
            {var subQ0=sQuery(id+"F0.wireOp",EDGE,"E35");var subQ1=sQuery(id+"F0.wireOp",EDGE,"E19");var subQ2=makeQuery(id+"F0.imprint","INTERSECT",VERTEX,{"derivedFrom":[sQuery(id+"F0.wireOp",EDGE,"E18"),subQ1,sQuery(id+"F0.wireOp",EDGE,"E21"),sQuery(id+"F0.wireOp",EDGE,"E27"),subQ0,sQuery(id+"F0.wireOp",EDGE,"E40")]});Q47=makeQuery(id+"F0.imprint","IMPRINT",FACE,{"disambiguationData":[TD([[makeQuery(id+"F0.imprint","IMPRINT",EDGE,{"disambiguationData":[TD([[subQ2,-1.0]])],"derivedFrom":subQ1}),1.0]])]});}
            var Q48;
            {var subQ0=sQuery(id+"F0.wireOp",EDGE,"E27");var subQ1=sQuery(id+"F0.wireOp",EDGE,"E19");var subQ2=makeQuery(id+"F0.imprint","INTERSECT",VERTEX,{"derivedFrom":[sQuery(id+"F0.wireOp",EDGE,"E3"),sQuery(id+"F0.wireOp",EDGE,"E9"),subQ1,sQuery(id+"F0.wireOp",EDGE,"E22"),sQuery(id+"F0.wireOp",EDGE,"E25"),subQ0]});Q48=makeQuery(id+"F0.imprint","IMPRINT",FACE,{"disambiguationData":[TD([[makeQuery(id+"F0.imprint","IMPRINT",EDGE,{"disambiguationData":[TD([[subQ2,-1.0]])],"derivedFrom":subQ1}),1.0]])]});}
            var Q49;
            {var subQ0=sQuery(id+"F0.wireOp",EDGE,"E32");var subQ1=sQuery(id+"F0.wireOp",EDGE,"E4");var subQ2=makeQuery(id+"F0.imprint","INTERSECT",VERTEX,{"derivedFrom":[subQ1,sQuery(id+"F0.wireOp",EDGE,"E5"),sQuery(id+"F0.wireOp",EDGE,"E10"),sQuery(id+"F0.wireOp",EDGE,"E17"),sQuery(id+"F0.wireOp",EDGE,"E31"),subQ0]});Q49=makeQuery(id+"F0.imprint","IMPRINT",FACE,{"disambiguationData":[TD([[makeQuery(id+"F0.imprint","IMPRINT",EDGE,{"disambiguationData":[TD([[subQ2,-1.0]])],"derivedFrom":subQ1}),1.0]])]});}
            var Q50;
            {var subQ0=sQuery(id+"F0.wireOp",EDGE,"E31");var subQ1=sQuery(id+"F0.wireOp",EDGE,"E5");var subQ2=makeQuery(id+"F0.imprint","INTERSECT",VERTEX,{"derivedFrom":[sQuery(id+"F0.wireOp",EDGE,"E4"),subQ1,sQuery(id+"F0.wireOp",EDGE,"E10"),sQuery(id+"F0.wireOp",EDGE,"E17"),subQ0,sQuery(id+"F0.wireOp",EDGE,"E32")]});Q50=makeQuery(id+"F0.imprint","IMPRINT",FACE,{"disambiguationData":[TD([[makeQuery(id+"F0.imprint","IMPRINT",EDGE,{"disambiguationData":[TD([[subQ2,1.0]])],"derivedFrom":subQ1}),1.0]])]});}
            var Q51;
            {var subQ0=sQuery(id+"F0.wireOp",EDGE,"E38");var subQ1=sQuery(id+"F0.wireOp",EDGE,"E11");var subQ2=makeQuery(id+"F0.imprint","INTERSECT",VERTEX,{"derivedFrom":[sQuery(id+"F0.wireOp",EDGE,"E10"),subQ1,sQuery(id+"F0.wireOp",EDGE,"E13"),sQuery(id+"F0.wireOp",EDGE,"E36"),subQ0]});Q51=makeQuery(id+"F0.imprint","IMPRINT",FACE,{"disambiguationData":[TD([[makeQuery(id+"F0.imprint","IMPRINT",EDGE,{"disambiguationData":[TD([[subQ2,-1.0]])],"derivedFrom":subQ1}),1.0]])]});}
            var Q52;
            {var subQ0=sQuery(id+"F0.wireOp",EDGE,"E41");var subQ1=sQuery(id+"F0.wireOp",EDGE,"E20");var subQ2=makeQuery(id+"F0.imprint","INTERSECT",VERTEX,{"derivedFrom":[sQuery(id+"F0.wireOp",EDGE,"E19"),subQ1,sQuery(id+"F0.wireOp",EDGE,"E22"),sQuery(id+"F0.wireOp",EDGE,"E28"),sQuery(id+"F0.wireOp",EDGE,"E35"),subQ0]});Q52=makeQuery(id+"F0.imprint","IMPRINT",FACE,{"disambiguationData":[TD([[makeQuery(id+"F0.imprint","IMPRINT",EDGE,{"disambiguationData":[TD([[subQ2,-1.0]])],"derivedFrom":subQ1}),1.0]])]});}
            var Q53;
            {var subQ0=sQuery(id+"F0.wireOp",EDGE,"E23");var subQ1=sQuery(id+"F0.wireOp",EDGE,"E21");var subQ2=makeQuery(id+"F0.imprint","INTERSECT",VERTEX,{"derivedFrom":[sQuery(id+"F0.wireOp",EDGE,"E2"),sQuery(id+"F0.wireOp",EDGE,"E15"),sQuery(id+"F0.wireOp",EDGE,"E19"),subQ1,subQ0,sQuery(id+"F0.wireOp",EDGE,"E28")]});Q53=makeQuery(id+"F0.imprint","IMPRINT",FACE,{"disambiguationData":[TD([[makeQuery(id+"F0.imprint","IMPRINT",EDGE,{"disambiguationData":[TD([[subQ2,1.0]])],"derivedFrom":subQ1}),1.0]])]});}
            var Q54;
            {var subQ0=sQuery(id+"F0.wireOp",EDGE,"E47");var subQ1=sQuery(id+"F0.wireOp",EDGE,"E20");var subQ2=makeQuery(id+"F0.imprint","INTERSECT",VERTEX,{"derivedFrom":[sQuery(id+"F0.wireOp",EDGE,"E15"),subQ1,sQuery(id+"F0.wireOp",EDGE,"E24"),sQuery(id+"F0.wireOp",EDGE,"E28"),sQuery(id+"F0.wireOp",EDGE,"E34"),subQ0]});Q54=makeQuery(id+"F0.imprint","IMPRINT",FACE,{"disambiguationData":[TD([[makeQuery(id+"F0.imprint","IMPRINT",EDGE,{"disambiguationData":[TD([[subQ2,1.0]])],"derivedFrom":subQ1}),1.0]])]});}
            var Q55;
            {var subQ0=sQuery(id+"F0.wireOp",EDGE,"E28");var subQ1=sQuery(id+"F0.wireOp",EDGE,"E15");var subQ2=makeQuery(id+"F0.imprint","INTERSECT",VERTEX,{"derivedFrom":[sQuery(id+"F0.wireOp",EDGE,"E2"),subQ1,sQuery(id+"F0.wireOp",EDGE,"E19"),sQuery(id+"F0.wireOp",EDGE,"E21"),sQuery(id+"F0.wireOp",EDGE,"E23"),subQ0]});Q55=makeQuery(id+"F0.imprint","IMPRINT",FACE,{"disambiguationData":[TD([[makeQuery(id+"F0.imprint","IMPRINT",EDGE,{"disambiguationData":[TD([[subQ2,-1.0]])],"derivedFrom":subQ1}),1.0]])]});}
            var Q56;
            {var subQ0=sQuery(id+"F0.wireOp",EDGE,"E24");var subQ1=sQuery(id+"F0.wireOp",EDGE,"E20");var subQ2=makeQuery(id+"F0.imprint","INTERSECT",VERTEX,{"derivedFrom":[sQuery(id+"F0.wireOp",EDGE,"E1"),sQuery(id+"F0.wireOp",EDGE,"E2"),sQuery(id+"F0.wireOp",EDGE,"E16"),subQ1,sQuery(id+"F0.wireOp",EDGE,"E23"),subQ0]});Q56=makeQuery(id+"F0.imprint","IMPRINT",FACE,{"disambiguationData":[TD([[makeQuery(id+"F0.imprint","IMPRINT",EDGE,{"disambiguationData":[TD([[subQ2,1.0]])],"derivedFrom":subQ1}),1.0]])]});}
            var Q57;
            {var subQ0=sQuery(id+"F0.wireOp",EDGE,"E34");var subQ1=sQuery(id+"F0.wireOp",EDGE,"E15");var subQ2=makeQuery(id+"F0.imprint","INTERSECT",VERTEX,{"derivedFrom":[subQ1,sQuery(id+"F0.wireOp",EDGE,"E16"),sQuery(id+"F0.wireOp",EDGE,"E23"),sQuery(id+"F0.wireOp",EDGE,"E33"),subQ0]});Q57=makeQuery(id+"F0.imprint","IMPRINT",FACE,{"disambiguationData":[TD([[makeQuery(id+"F0.imprint","IMPRINT",EDGE,{"disambiguationData":[TD([[subQ2,1.0]])],"derivedFrom":subQ1}),1.0]])]});}
            var Q58;
            {var subQ0=sQuery(id+"F0.wireOp",EDGE,"E23");var subQ1=sQuery(id+"F0.wireOp",EDGE,"E16");var subQ2=makeQuery(id+"F0.imprint","INTERSECT",VERTEX,{"derivedFrom":[sQuery(id+"F0.wireOp",EDGE,"E15"),subQ1,subQ0,sQuery(id+"F0.wireOp",EDGE,"E33"),sQuery(id+"F0.wireOp",EDGE,"E34")]});Q58=makeQuery(id+"F0.imprint","IMPRINT",FACE,{"disambiguationData":[TD([[makeQuery(id+"F0.imprint","IMPRINT",EDGE,{"disambiguationData":[TD([[subQ2,1.0]])],"derivedFrom":subQ1}),1.0]])]});}
            var Q59;
            {var subQ0=sQuery(id+"F0.wireOp",EDGE,"E33");var subQ1=sQuery(id+"F0.wireOp",EDGE,"E15");var subQ2=makeQuery(id+"F0.imprint","INTERSECT",VERTEX,{"derivedFrom":[subQ1,sQuery(id+"F0.wireOp",EDGE,"E16"),sQuery(id+"F0.wireOp",EDGE,"E23"),subQ0,sQuery(id+"F0.wireOp",EDGE,"E34")]});Q59=makeQuery(id+"F0.imprint","IMPRINT",FACE,{"disambiguationData":[TD([[makeQuery(id+"F0.imprint","IMPRINT",EDGE,{"disambiguationData":[TD([[subQ2,-1.0]])],"derivedFrom":subQ1}),1.0]])]});}
            var Q60;
            {var subQ0=sQuery(id+"F0.wireOp",EDGE,"E40");var subQ1=sQuery(id+"F0.wireOp",EDGE,"E18");var subQ2=makeQuery(id+"F0.imprint","INTERSECT",VERTEX,{"derivedFrom":[subQ1,sQuery(id+"F0.wireOp",EDGE,"E22"),sQuery(id+"F0.wireOp",EDGE,"E25"),subQ0,sQuery(id+"F0.wireOp",EDGE,"4keGgqQS-VjFO-Uu6F-eGOx-LwLd6920sbIl"),sQuery(id+"F0.wireOp",EDGE,"E43")]});Q60=makeQuery(id+"F0.imprint","IMPRINT",FACE,{"disambiguationData":[TD([[makeQuery(id+"F0.imprint","IMPRINT",EDGE,{"disambiguationData":[TD([[subQ2,-1.0]])],"derivedFrom":subQ1}),1.0]])]});}
            var Q61;
            {var subQ0=sQuery(id+"F0.wireOp",EDGE,"E25");var subQ1=sQuery(id+"F0.wireOp",EDGE,"E22");var subQ2=makeQuery(id+"F0.imprint","INTERSECT",VERTEX,{"derivedFrom":[sQuery(id+"F0.wireOp",EDGE,"E3"),sQuery(id+"F0.wireOp",EDGE,"E9"),sQuery(id+"F0.wireOp",EDGE,"E19"),subQ1,subQ0,sQuery(id+"F0.wireOp",EDGE,"E27")]});Q61=makeQuery(id+"F0.imprint","IMPRINT",FACE,{"disambiguationData":[TD([[makeQuery(id+"F0.imprint","IMPRINT",EDGE,{"disambiguationData":[TD([[subQ2,-1.0]])],"derivedFrom":subQ1}),1.0]])]});}
            var Q62;
            {var subQ0=sQuery(id+"F0.wireOp",EDGE,"E27");var subQ1=sQuery(id+"F0.wireOp",EDGE,"E9");var subQ2=makeQuery(id+"F0.imprint","INTERSECT",VERTEX,{"derivedFrom":[sQuery(id+"F0.wireOp",EDGE,"E3"),subQ1,sQuery(id+"F0.wireOp",EDGE,"E19"),sQuery(id+"F0.wireOp",EDGE,"E22"),sQuery(id+"F0.wireOp",EDGE,"E25"),subQ0]});Q62=makeQuery(id+"F0.imprint","IMPRINT",FACE,{"disambiguationData":[TD([[makeQuery(id+"F0.imprint","IMPRINT",EDGE,{"disambiguationData":[TD([[subQ2,1.0]])],"derivedFrom":subQ1}),1.0]])]});}
            var Q63;
            {var subQ0=sQuery(id+"F0.wireOp",EDGE,"E43");var subQ1=sQuery(id+"F0.wireOp",EDGE,"E18");var subQ2=makeQuery(id+"F0.imprint","INTERSECT",VERTEX,{"derivedFrom":[sQuery(id+"F0.wireOp",EDGE,"E9"),subQ1,sQuery(id+"F0.wireOp",EDGE,"E26"),sQuery(id+"F0.wireOp",EDGE,"E27"),sQuery(id+"F0.wireOp",EDGE,"E42"),subQ0]});Q63=makeQuery(id+"F0.imprint","IMPRINT",FACE,{"disambiguationData":[TD([[makeQuery(id+"F0.imprint","IMPRINT",EDGE,{"disambiguationData":[TD([[subQ2,-1.0]])],"derivedFrom":subQ1}),1.0]])]});}
            var Q64;
            {var subQ0=sQuery(id+"F0.wireOp",EDGE,"E26");var subQ1=sQuery(id+"F0.wireOp",EDGE,"E18");var subQ2=makeQuery(id+"F0.imprint","INTERSECT",VERTEX,{"derivedFrom":[sQuery(id+"F0.wireOp",EDGE,"E3"),sQuery(id+"F0.wireOp",EDGE,"E4"),sQuery(id+"F0.wireOp",EDGE,"E17"),subQ1,sQuery(id+"F0.wireOp",EDGE,"E25"),subQ0]});Q64=makeQuery(id+"F0.imprint","IMPRINT",FACE,{"disambiguationData":[TD([[makeQuery(id+"F0.imprint","IMPRINT",EDGE,{"disambiguationData":[TD([[subQ2,-1.0]])],"derivedFrom":subQ1}),1.0]])]});}
            var Q65;
            {var subQ0=sQuery(id+"F0.wireOp",EDGE,"E42");var subQ1=sQuery(id+"F0.wireOp",EDGE,"E9");var subQ2=makeQuery(id+"F0.imprint","INTERSECT",VERTEX,{"derivedFrom":[subQ1,sQuery(id+"F0.wireOp",EDGE,"E17"),sQuery(id+"F0.wireOp",EDGE,"E25"),sQuery(id+"F0.wireOp",EDGE,"E39"),subQ0]});Q65=makeQuery(id+"F0.imprint","IMPRINT",FACE,{"disambiguationData":[TD([[makeQuery(id+"F0.imprint","IMPRINT",EDGE,{"disambiguationData":[TD([[subQ2,-1.0]])],"derivedFrom":subQ1}),1.0]])]});}
            var Q66;
            {var subQ0=sQuery(id+"F0.wireOp",EDGE,"E25");var subQ1=sQuery(id+"F0.wireOp",EDGE,"E17");var subQ2=makeQuery(id+"F0.imprint","INTERSECT",VERTEX,{"derivedFrom":[sQuery(id+"F0.wireOp",EDGE,"E9"),subQ1,subQ0,sQuery(id+"F0.wireOp",EDGE,"E39"),sQuery(id+"F0.wireOp",EDGE,"E42")]});Q66=makeQuery(id+"F0.imprint","IMPRINT",FACE,{"disambiguationData":[TD([[makeQuery(id+"F0.imprint","IMPRINT",EDGE,{"disambiguationData":[TD([[subQ2,-1.0]])],"derivedFrom":subQ1}),1.0]])]});}
            var Q67;
            {var subQ0=sQuery(id+"F0.wireOp",EDGE,"E39");var subQ1=sQuery(id+"F0.wireOp",EDGE,"E9");var subQ2=makeQuery(id+"F0.imprint","INTERSECT",VERTEX,{"derivedFrom":[subQ1,sQuery(id+"F0.wireOp",EDGE,"E17"),sQuery(id+"F0.wireOp",EDGE,"E25"),subQ0,sQuery(id+"F0.wireOp",EDGE,"E42")]});Q67=makeQuery(id+"F0.imprint","IMPRINT",FACE,{"disambiguationData":[TD([[makeQuery(id+"F0.imprint","IMPRINT",EDGE,{"disambiguationData":[TD([[subQ2,1.0]])],"derivedFrom":subQ1}),1.0]])]});}
            var Q68;
            {var subQ0=sQuery(id+"F0.wireOp",EDGE,"E49");var subQ1=sQuery(id+"F0.wireOp",EDGE,"E17");var subQ2=makeQuery(id+"F0.imprint","INTERSECT",VERTEX,{"derivedFrom":[subQ1,sQuery(id+"F0.wireOp",EDGE,"E26"),sQuery(id+"F0.wireOp",EDGE,"E32"),sQuery(id+"F0.wireOp",EDGE,"E44"),subQ0]});Q68=makeQuery(id+"F0.imprint","IMPRINT",FACE,{"disambiguationData":[TD([[makeQuery(id+"F0.imprint","IMPRINT",EDGE,{"disambiguationData":[TD([[subQ2,-1.0]])],"derivedFrom":subQ1}),1.0]])]});}
            var Q69;
            {var subQ0=sQuery(id+"F0.wireOp",EDGE,"E32");var subQ1=sQuery(id+"F0.wireOp",EDGE,"E26");var subQ2=makeQuery(id+"F0.imprint","INTERSECT",VERTEX,{"derivedFrom":[sQuery(id+"F0.wireOp",EDGE,"E17"),subQ1,subQ0,sQuery(id+"F0.wireOp",EDGE,"E44"),sQuery(id+"F0.wireOp",EDGE,"E49")]});Q69=makeQuery(id+"F0.imprint","IMPRINT",FACE,{"disambiguationData":[TD([[makeQuery(id+"F0.imprint","IMPRINT",EDGE,{"disambiguationData":[TD([[subQ2,1.0]])],"derivedFrom":subQ1}),1.0]])]});}
            var Q70;
            {var subQ0=sQuery(id+"F0.wireOp",EDGE,"E44");var subQ1=sQuery(id+"F0.wireOp",EDGE,"E17");var subQ2=makeQuery(id+"F0.imprint","INTERSECT",VERTEX,{"derivedFrom":[subQ1,sQuery(id+"F0.wireOp",EDGE,"E26"),sQuery(id+"F0.wireOp",EDGE,"E32"),subQ0,sQuery(id+"F0.wireOp",EDGE,"E49")]});Q70=makeQuery(id+"F0.imprint","IMPRINT",FACE,{"disambiguationData":[TD([[makeQuery(id+"F0.imprint","IMPRINT",EDGE,{"disambiguationData":[TD([[subQ2,1.0]])],"derivedFrom":subQ1}),1.0]])]});}
            var Q71;
            {var subQ0=sQuery(id+"F0.wireOp",EDGE,"E39");var subQ1=sQuery(id+"F0.wireOp",EDGE,"E8");var subQ2=makeQuery(id+"F0.imprint","INTERSECT",VERTEX,{"derivedFrom":[sQuery(id+"F0.wireOp",EDGE,"E4"),subQ1,sQuery(id+"F0.wireOp",EDGE,"E9"),sQuery(id+"F0.wireOp",EDGE,"E26"),sQuery(id+"F0.wireOp",EDGE,"E32"),subQ0]});Q71=makeQuery(id+"F0.imprint","IMPRINT",FACE,{"disambiguationData":[TD([[makeQuery(id+"F0.imprint","IMPRINT",EDGE,{"disambiguationData":[TD([[subQ2,1.0]])],"derivedFrom":subQ1}),1.0]])]});}
            var Q72;
            {var subQ0=sQuery(id+"F0.wireOp",EDGE,"E31");var subQ1=sQuery(id+"F0.wireOp",EDGE,"E17");var subQ2=makeQuery(id+"F0.imprint","INTERSECT",VERTEX,{"derivedFrom":[sQuery(id+"F0.wireOp",EDGE,"E4"),sQuery(id+"F0.wireOp",EDGE,"E5"),sQuery(id+"F0.wireOp",EDGE,"E10"),subQ1,subQ0,sQuery(id+"F0.wireOp",EDGE,"E32")]});Q72=makeQuery(id+"F0.imprint","IMPRINT",FACE,{"disambiguationData":[TD([[makeQuery(id+"F0.imprint","IMPRINT",EDGE,{"disambiguationData":[TD([[subQ2,-1.0]])],"derivedFrom":subQ1}),1.0]])]});}
            var Q73;
            {var subQ0=sQuery(id+"F0.wireOp",EDGE,"E45");var subQ1=sQuery(id+"F0.wireOp",EDGE,"E8");var subQ2=makeQuery(id+"F0.imprint","INTERSECT",VERTEX,{"derivedFrom":[subQ1,sQuery(id+"F0.wireOp",EDGE,"E10"),sQuery(id+"F0.wireOp",EDGE,"E32"),sQuery(id+"F0.wireOp",EDGE,"E38"),subQ0,sQuery(id+"F0.wireOp",EDGE,"E46")]});Q73=makeQuery(id+"F0.imprint","IMPRINT",FACE,{"disambiguationData":[TD([[makeQuery(id+"F0.imprint","IMPRINT",EDGE,{"disambiguationData":[TD([[subQ2,-1.0]])],"derivedFrom":subQ1}),1.0]])]});}
            var Q74;
            {var subQ0=sQuery(id+"F0.wireOp",EDGE,"E32");var subQ1=sQuery(id+"F0.wireOp",EDGE,"E10");var subQ2=makeQuery(id+"F0.imprint","INTERSECT",VERTEX,{"derivedFrom":[sQuery(id+"F0.wireOp",EDGE,"E4"),sQuery(id+"F0.wireOp",EDGE,"E5"),subQ1,sQuery(id+"F0.wireOp",EDGE,"E17"),sQuery(id+"F0.wireOp",EDGE,"E31"),subQ0]});Q74=makeQuery(id+"F0.imprint","IMPRINT",FACE,{"disambiguationData":[TD([[makeQuery(id+"F0.imprint","IMPRINT",EDGE,{"disambiguationData":[TD([[subQ2,1.0]])],"derivedFrom":subQ1}),1.0]])]});}
            var Q75;
            {var subQ0=sQuery(id+"F0.wireOp",EDGE,"E38");var subQ1=sQuery(id+"F0.wireOp",EDGE,"E8");var subQ2=makeQuery(id+"F0.imprint","INTERSECT",VERTEX,{"derivedFrom":[sQuery(id+"F0.wireOp",EDGE,"E5"),subQ1,sQuery(id+"F0.wireOp",EDGE,"E11"),sQuery(id+"F0.wireOp",EDGE,"E14"),sQuery(id+"F0.wireOp",EDGE,"E31"),subQ0]});Q75=makeQuery(id+"F0.imprint","IMPRINT",FACE,{"disambiguationData":[TD([[makeQuery(id+"F0.imprint","IMPRINT",EDGE,{"disambiguationData":[TD([[subQ2,-1.0]])],"derivedFrom":subQ1}),1.0]])]});}
            var Q76;
            {var subQ0=sQuery(id+"F0.wireOp",EDGE,"E46");var subQ1=sQuery(id+"F0.wireOp",EDGE,"E10");var subQ2=makeQuery(id+"F0.imprint","INTERSECT",VERTEX,{"derivedFrom":[subQ1,sQuery(id+"F0.wireOp",EDGE,"E14"),sQuery(id+"F0.wireOp",EDGE,"E31"),subQ0,sQuery(id+"F0.wireOp",EDGE,"E48")]});Q76=makeQuery(id+"F0.imprint","IMPRINT",FACE,{"disambiguationData":[TD([[makeQuery(id+"F0.imprint","IMPRINT",EDGE,{"disambiguationData":[TD([[subQ2,-1.0]])],"derivedFrom":subQ1}),1.0]])]});}
            var Q77;
            {var subQ0=sQuery(id+"F0.wireOp",EDGE,"E31");var subQ1=sQuery(id+"F0.wireOp",EDGE,"E14");var subQ2=makeQuery(id+"F0.imprint","INTERSECT",VERTEX,{"derivedFrom":[sQuery(id+"F0.wireOp",EDGE,"E10"),subQ1,subQ0,sQuery(id+"F0.wireOp",EDGE,"E46"),sQuery(id+"F0.wireOp",EDGE,"E48")]});Q77=makeQuery(id+"F0.imprint","IMPRINT",FACE,{"disambiguationData":[TD([[makeQuery(id+"F0.imprint","IMPRINT",EDGE,{"disambiguationData":[TD([[subQ2,-1.0]])],"derivedFrom":subQ1}),1.0]])]});}
            var Q78;
            {var subQ0=sQuery(id+"F0.wireOp",EDGE,"E48");var subQ1=sQuery(id+"F0.wireOp",EDGE,"E10");var subQ2=makeQuery(id+"F0.imprint","INTERSECT",VERTEX,{"derivedFrom":[subQ1,sQuery(id+"F0.wireOp",EDGE,"E14"),sQuery(id+"F0.wireOp",EDGE,"E31"),sQuery(id+"F0.wireOp",EDGE,"E46"),subQ0]});Q78=makeQuery(id+"F0.imprint","IMPRINT",FACE,{"disambiguationData":[TD([[makeQuery(id+"F0.imprint","IMPRINT",EDGE,{"disambiguationData":[TD([[subQ2,1.0]])],"derivedFrom":subQ1}),1.0]])]});}
            var Q79;
            {var subQ0=sQuery(id+"F0.wireOp",EDGE,"E50");var subQ1=sQuery(id+"F0.wireOp",EDGE,"E12");var subQ2=makeQuery(id+"F0.imprint","INTERSECT",VERTEX,{"derivedFrom":[subQ1,sQuery(id+"F0.wireOp",EDGE,"E13"),sQuery(id+"F0.wireOp",EDGE,"E29"),subQ0]});Q79=makeQuery(id+"F0.imprint","IMPRINT",FACE,{"disambiguationData":[TD([[makeQuery(id+"F0.imprint","IMPRINT",EDGE,{"disambiguationData":[TD([[subQ2,-1.0]])],"derivedFrom":subQ1}),1.0]])]});}
            var Q80;
            {var subQ0=sQuery(id+"F0.wireOp",EDGE,"E29");var subQ1=sQuery(id+"F0.wireOp",EDGE,"E13");var subQ2=makeQuery(id+"F0.imprint","INTERSECT",VERTEX,{"derivedFrom":[sQuery(id+"F0.wireOp",EDGE,"E12"),subQ1,subQ0,sQuery(id+"F0.wireOp",EDGE,"E50")]});Q80=makeQuery(id+"F0.imprint","IMPRINT",FACE,{"disambiguationData":[TD([[makeQuery(id+"F0.imprint","IMPRINT",EDGE,{"disambiguationData":[TD([[subQ2,1.0]])],"derivedFrom":subQ1}),1.0]])]});}
            var Q81;
            {var subQ0=sQuery(id+"F0.wireOp",EDGE,"E37");var subQ1=sQuery(id+"F0.wireOp",EDGE,"E7");var subQ2=makeQuery(id+"F0.imprint","INTERSECT",VERTEX,{"derivedFrom":[subQ1,sQuery(id+"F0.wireOp",EDGE,"E12"),sQuery(id+"F0.wireOp",EDGE,"E30"),subQ0]});Q81=makeQuery(id+"F0.imprint","IMPRINT",FACE,{"disambiguationData":[TD([[makeQuery(id+"F0.imprint","IMPRINT",EDGE,{"disambiguationData":[TD([[subQ2,-1.0]])],"derivedFrom":subQ1}),1.0]])]});}
            var Q82;
            {var subQ0=sQuery(id+"F0.wireOp",EDGE,"E30");var subQ1=sQuery(id+"F0.wireOp",EDGE,"E12");var subQ2=makeQuery(id+"F0.imprint","INTERSECT",VERTEX,{"derivedFrom":[sQuery(id+"F0.wireOp",EDGE,"E7"),subQ1,subQ0,sQuery(id+"F0.wireOp",EDGE,"E37")]});Q82=makeQuery(id+"F0.imprint","IMPRINT",FACE,{"disambiguationData":[TD([[makeQuery(id+"F0.imprint","IMPRINT",EDGE,{"disambiguationData":[TD([[subQ2,1.0]])],"derivedFrom":subQ1}),1.0]])]});}
            var Q83;
            {var subQ0=sQuery(id+"F0.wireOp",EDGE,"E29");var subQ1=sQuery(id+"F0.wireOp",EDGE,"E16");var subQ2=makeQuery(id+"F0.imprint","INTERSECT",VERTEX,{"derivedFrom":[sQuery(id+"F0.wireOp",EDGE,"E7"),subQ1,subQ0,sQuery(id+"F0.wireOp",EDGE,"E33")]});Q83=makeQuery(id+"F0.imprint","IMPRINT",FACE,{"disambiguationData":[TD([[makeQuery(id+"F0.imprint","IMPRINT",EDGE,{"disambiguationData":[TD([[subQ2,-1.0]])],"derivedFrom":subQ1}),1.0]])]});}
            var Q84;
            {var subQ0=sQuery(id+"F0.wireOp",EDGE,"E33");var subQ1=sQuery(id+"F0.wireOp",EDGE,"E7");var subQ2=makeQuery(id+"F0.imprint","INTERSECT",VERTEX,{"derivedFrom":[subQ1,sQuery(id+"F0.wireOp",EDGE,"E16"),sQuery(id+"F0.wireOp",EDGE,"E29"),subQ0]});Q84=makeQuery(id+"F0.imprint","IMPRINT",FACE,{"disambiguationData":[TD([[makeQuery(id+"F0.imprint","IMPRINT",EDGE,{"disambiguationData":[TD([[subQ2,1.0]])],"derivedFrom":subQ1}),1.0]])]});}
            var Q85;
            {var subQ0=sQuery(id+"F0.wireOp",EDGE,"E30");var subQ1=sQuery(id+"F0.wireOp",EDGE,"E24");var subQ2=makeQuery(id+"F0.imprint","INTERSECT",VERTEX,{"derivedFrom":[sQuery(id+"F0.wireOp",EDGE,"E16"),subQ1,subQ0,sQuery(id+"F0.wireOp",EDGE,"E51")]});Q85=makeQuery(id+"F0.imprint","IMPRINT",FACE,{"disambiguationData":[TD([[makeQuery(id+"F0.imprint","IMPRINT",EDGE,{"disambiguationData":[TD([[subQ2,-1.0]])],"derivedFrom":subQ1}),1.0]])]});}
            var Q86;
            {var subQ0=sQuery(id+"F0.wireOp",EDGE,"E51");var subQ1=sQuery(id+"F0.wireOp",EDGE,"E16");var subQ2=makeQuery(id+"F0.imprint","INTERSECT",VERTEX,{"derivedFrom":[subQ1,sQuery(id+"F0.wireOp",EDGE,"E24"),sQuery(id+"F0.wireOp",EDGE,"E30"),subQ0]});Q86=makeQuery(id+"F0.imprint","IMPRINT",FACE,{"disambiguationData":[TD([[makeQuery(id+"F0.imprint","IMPRINT",EDGE,{"disambiguationData":[TD([[subQ2,1.0]])],"derivedFrom":subQ1}),1.0]])]});}
            var Q87;
            {var subQ0=sQuery(id+"F0.wireOp",EDGE,"E52");var subQ1=sQuery(id+"F0.wireOp",EDGE,"E12");var subQ2=makeQuery(id+"F0.imprint","INTERSECT",VERTEX,{"derivedFrom":[sQuery(id+"F0.wireOp",EDGE,"E7"),subQ1,sQuery(id+"F0.wireOp",EDGE,"E30"),sQuery(id+"F0.wireOp",EDGE,"E37"),subQ0,sQuery(id+"F0.wireOp",EDGE,"E53")]});Q87=makeQuery(id+"F0.imprint","IMPRINT",FACE,{"disambiguationData":[TD([[makeQuery(id+"F0.imprint","IMPRINT",EDGE,{"disambiguationData":[TD([[subQ2,-1.0]])],"derivedFrom":subQ1}),1.0]])]});}
            var Q88;
            {var subQ0=sQuery(id+"F0.wireOp",EDGE,"E53");var subQ1=sQuery(id+"F0.wireOp",EDGE,"E7");var subQ2=makeQuery(id+"F0.imprint","INTERSECT",VERTEX,{"derivedFrom":[subQ1,sQuery(id+"F0.wireOp",EDGE,"E12"),sQuery(id+"F0.wireOp",EDGE,"E30"),sQuery(id+"F0.wireOp",EDGE,"E37"),sQuery(id+"F0.wireOp",EDGE,"E52"),subQ0]});Q88=makeQuery(id+"F0.imprint","IMPRINT",FACE,{"disambiguationData":[TD([[makeQuery(id+"F0.imprint","IMPRINT",EDGE,{"disambiguationData":[TD([[subQ2,1.0]])],"derivedFrom":subQ1}),1.0]])]});}
            var Q89;
            {var subQ0=sQuery(id+"F0.wireOp",EDGE,"E54");var subQ1=sQuery(id+"F0.wireOp",EDGE,"E16");var subQ2=makeQuery(id+"F0.imprint","INTERSECT",VERTEX,{"derivedFrom":[sQuery(id+"F0.wireOp",EDGE,"E7"),subQ1,sQuery(id+"F0.wireOp",EDGE,"E29"),sQuery(id+"F0.wireOp",EDGE,"E33"),sQuery(id+"F0.wireOp",EDGE,"E53"),subQ0]});Q89=makeQuery(id+"F0.imprint","IMPRINT",FACE,{"disambiguationData":[TD([[makeQuery(id+"F0.imprint","IMPRINT",EDGE,{"disambiguationData":[TD([[subQ2,1.0]])],"derivedFrom":subQ1}),1.0]])]});}
            extrude(context, id + "F1", {"entities" : qUnion([Q0, Q1, Q2, Q3, Q4, Q5, Q6, Q7, Q8, Q9, Q10, Q11, Q12, Q13, Q14, Q15, Q16, Q17, Q18, Q19, Q20, Q21, Q22, Q23, Q24, Q25, Q26, Q27, Q28, Q29, Q30, Q31, Q32, Q33, Q34, Q35, Q36, Q37, Q38, Q39, Q40, Q41, Q42, Q43, Q44, Q45, Q46, Q47, Q48, Q49, Q50, Q51, Q52, Q53, Q54, Q55, Q56, Q57, Q58, Q59, Q60, Q61, Q62, Q63, Q64, Q65, Q66, Q67, Q68, Q69, Q70, Q71, Q72, Q73, Q74, Q75, Q76, Q77, Q78, Q79, Q80, Q81, Q82, Q83, Q84, Q85, Q86, Q87, Q88, Q89]), "depth" : 4 * mm, "offsetDistance" : 25 * mm});
        }
        {
            var Q0;
            Q0=qCreatedBy(makeId("Top.planeOp"),FACE);
            var sketch = newSketch(context, id + "F2", { "sketchPlane" : qUnion([Q0])});
            skCircle(sketch, "E55", {"center": v(0, 0) * mm, "radius": 45 * mm});
            skSolve(sketch);
        }
        {
            var Q0;
            Q0=makeQuery(id+"F2.imprint","IMPRINT",FACE,{"disambiguationData":[TD([[makeQuery(id+"F2.imprint","IMPRINT",EDGE,{"derivedFrom":sQuery(id+"F2.wireOp",EDGE,"E55")}),1.0]])]});
            extrude(context, id + "F3", {"entities" : qUnion([Q0]), "depth" : -2 * mm, "offsetDistance" : 25 * mm});
        }
    });
